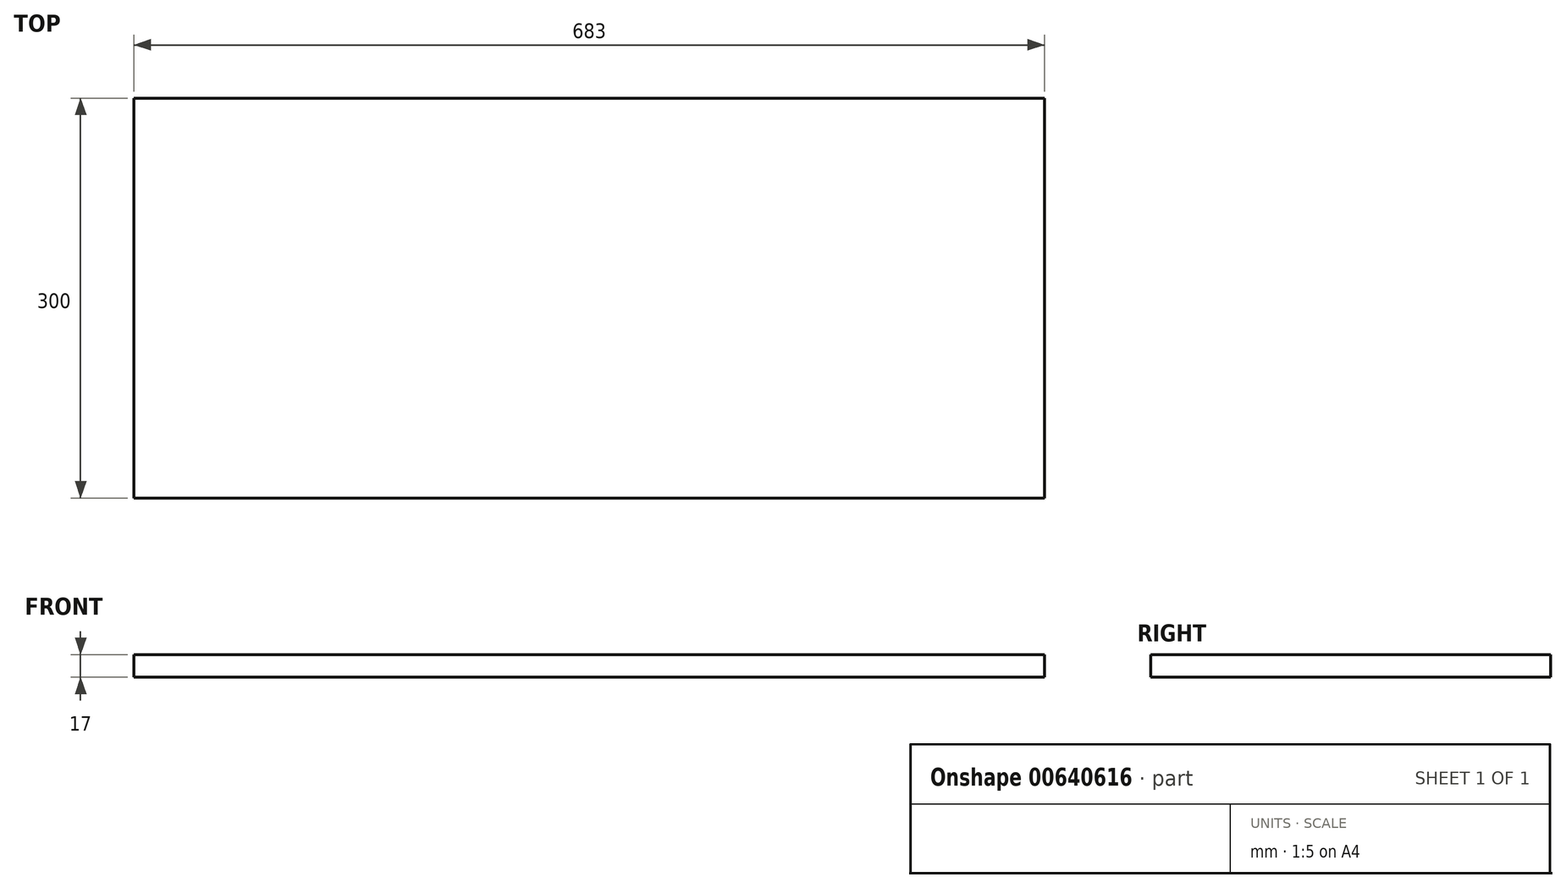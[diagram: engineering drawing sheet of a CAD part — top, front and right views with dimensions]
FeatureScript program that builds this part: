
annotation { "Feature Type Name" : "Feature", "Feature Type Description" : "" }
export const myFeature = defineFeature(function(context is Context, id is Id, definition is map)
    precondition{}
    {
        {
            var Q0;
            Q0=qCreatedBy(makeId("Top.planeOp"),FACE);
            var sketch = newSketch(context, id + "F0", { "sketchPlane" : qUnion([Q0])});
            skLineSegment(sketch, "E0.bottom", {"start": v(0, 0) * mm, "end": v(-683, 0) * mm});
            skLineSegment(sketch, "E0.top", {"start": v(0, 300) * mm, "end": v(-683, 300) * mm});
            skLineSegment(sketch, "E0.left", {"start": v(0, 0) * mm, "end": v(0, 300) * mm});
            skLineSegment(sketch, "E0.right", {"start": v(-683, 0) * mm, "end": v(-683, 300) * mm});
            skSolve(sketch);
        }
        {
            var Q0;
            Q0 = qSketchRegion(id + "F0", true);
            extrude(context, id + "F1", {"entities" : qUnion([Q0]), "depth" : 17 * mm, "offsetDistance" : 25 * mm});
        }
    });
